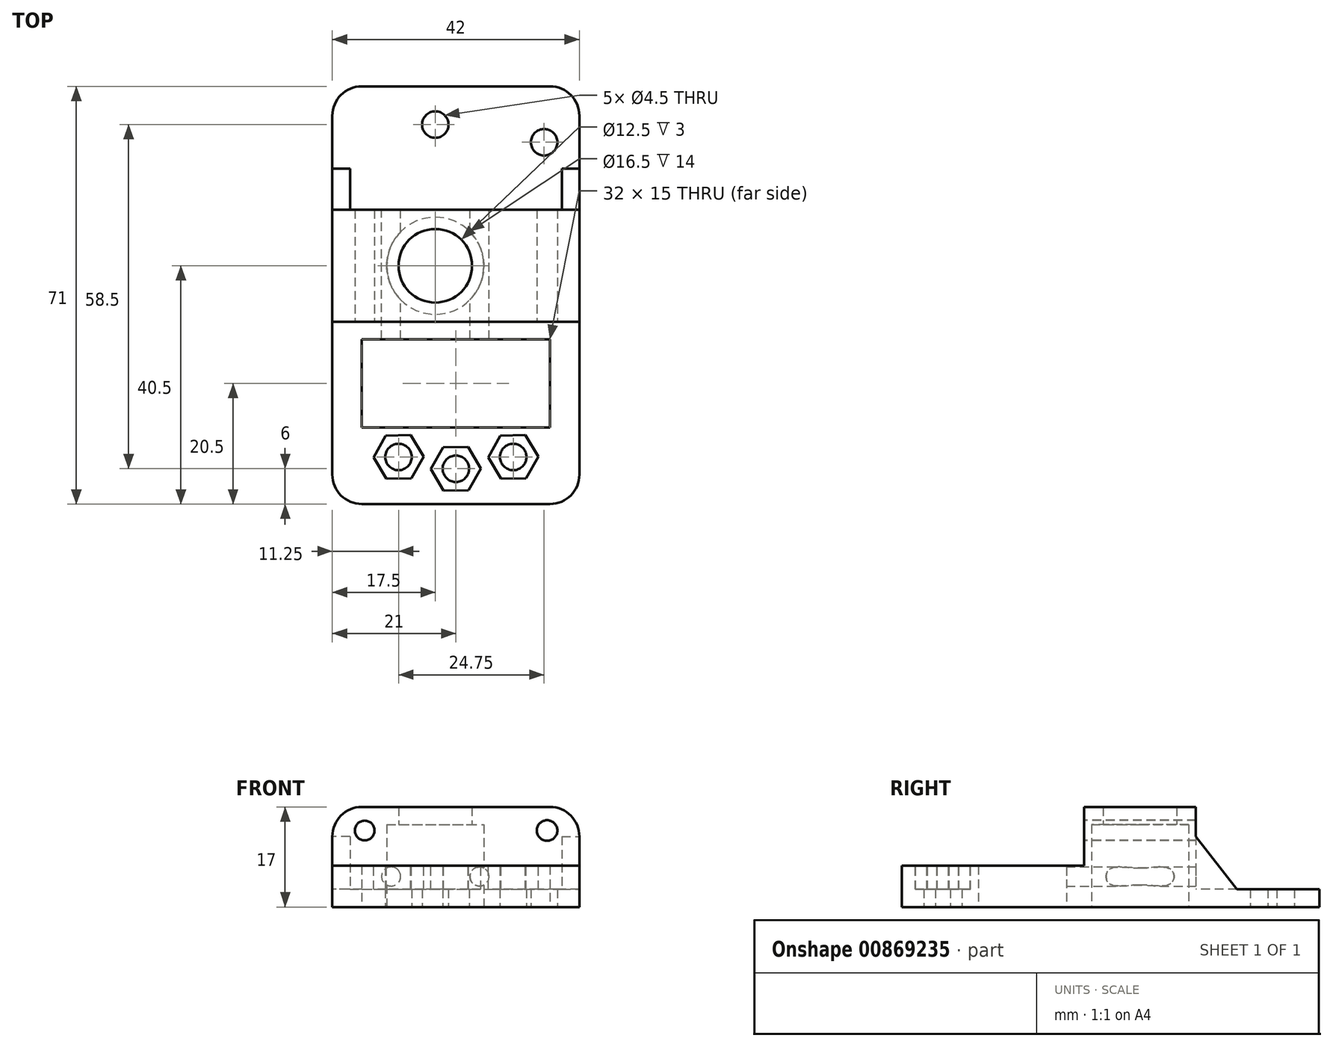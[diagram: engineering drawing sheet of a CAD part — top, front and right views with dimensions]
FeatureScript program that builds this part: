
annotation { "Feature Type Name" : "Feature", "Feature Type Description" : "" }
export const myFeature = defineFeature(function(context is Context, id is Id, definition is map)
    precondition{}
    {
        {
            var Q0;
            Q0=qCreatedBy(makeId("Top.planeOp"),FACE);
            var sketch = newSketch(context, id + "F0", { "sketchPlane" : qUnion([Q0])});
            skLineSegment(sketch, "E0.bottom", {"start": v(-21, 40) * mm, "end": v(21, 40) * mm});
            skLineSegment(sketch, "E0.top", {"start": v(-21, -31) * mm, "end": v(21, -31) * mm});
            skLineSegment(sketch, "E0.left", {"start": v(-21, 40) * mm, "end": v(-21, -31) * mm});
            skLineSegment(sketch, "E0.right", {"start": v(21, 40) * mm, "end": v(21, -31) * mm});
            skLineSegment(sketch, "E1", {"start": v(21, 0) * mm, "end": v(-21, 0) * mm});
            skLineSegment(sketch, "E2", {"start": v(-21, 19) * mm, "end": v(21, 19) * mm});
            skLineSegment(sketch, "E3.bottom", {"start": v(-16, -3) * mm, "end": v(16, -3) * mm});
            skLineSegment(sketch, "E3.top", {"start": v(-16, -18) * mm, "end": v(16, -18) * mm});
            skLineSegment(sketch, "E3.left", {"start": v(-16, -3) * mm, "end": v(-16, -18) * mm});
            skLineSegment(sketch, "E3.right", {"start": v(16, -3) * mm, "end": v(16, -18) * mm});
            skCircle(sketch, "E4", {"center": v(0, -25) * mm, "radius": 2.25 * mm});
            skCircle(sketch, "E5", {"center": v(-9.75, -23) * mm, "radius": 2.25 * mm});
            skCircle(sketch, "E6", {"center": v(9.75, -23) * mm, "radius": 2.25 * mm});
            skCircle(sketch, "E7", {"center": v(-3.5, 33.5) * mm, "radius": 2.25 * mm});
            skCircle(sketch, "E8", {"center": v(15, 30.5) * mm, "radius": 2.25 * mm});
            skLineSegment(sketch, "E9", {"start": v(-21, 9.5) * mm, "end": v(21, 9.5) * mm, "construction": true});
            skSolve(sketch);
        }
        {
            var Q0;
            {var subQ0=sQuery(id+"F0.wireOp",EDGE,"E0.top");Q0=makeQuery(id+"F0.imprint","IMPRINT",FACE,{"disambiguationData":[TD([[makeQuery(id+"F0.imprint","IMPRINT",EDGE,{"derivedFrom":subQ0}),1.0]])]});}
            extrude(context, id + "F1", {"entities" : qUnion([Q0]), "depth" : 7 * mm, "offsetDistance" : 25 * mm});
        }
        {
            var Q0;
            {var subQ0=sQuery(id+"F0.wireOp",EDGE,"E0.bottom");Q0=makeQuery(id+"F0.imprint","IMPRINT",FACE,{"disambiguationData":[TD([[makeQuery(id+"F0.imprint","IMPRINT",EDGE,{"derivedFrom":subQ0}),-1.0]])]});}
            extrude(context, id + "F2", {"entities" : qUnion([Q0]), "depth" : 3 * mm, "offsetDistance" : 25 * mm});
        }
        {
            var Q0;
            {var subQ0=sQuery(id+"F0.wireOp",EDGE,"E1");Q0=makeQuery(id+"F0.imprint","IMPRINT",FACE,{"disambiguationData":[TD([[makeQuery(id+"F0.imprint","IMPRINT",EDGE,{"derivedFrom":subQ0}),-1.0]])]});}
            extrude(context, id + "F3", {"entities" : qUnion([Q0]), "operationType" : NewBodyOperationType.ADD, "depth" : 17 * mm, "offsetDistance" : 25 * mm});
        }
        {
            var Q0;
            Q0=makeQuery(id+"F1.opExtrude","SWEPT_EDGE",EDGE,{"disambiguationData":[OSD([sQuery(id+"F0.wireOp",EDGE,"E0.top"),sQuery(id+"F0.wireOp",EDGE,"E0.left")])]});
            var Q1;
            Q1=makeQuery(id+"F1.opExtrude","SWEPT_EDGE",EDGE,{"disambiguationData":[OSD([sQuery(id+"F0.wireOp",EDGE,"E0.top"),sQuery(id+"F0.wireOp",EDGE,"E0.right")])]});
            fillet(context, id + "F4", {"entities" : qUnion([Q0, Q1]), "radius" : 5 * mm, "tangentPropagation" : true, "allowEdgeOverflow" : false});
        }
        {
            var Q0;
            Q0=makeQuery(id+"F2.opExtrude","SWEPT_EDGE",EDGE,{"disambiguationData":[OSD([sQuery(id+"F0.wireOp",EDGE,"E0.bottom"),sQuery(id+"F0.wireOp",EDGE,"E0.left")])]});
            var Q1;
            Q1=makeQuery(id+"F2.opExtrude","SWEPT_EDGE",EDGE,{"disambiguationData":[OSD([sQuery(id+"F0.wireOp",EDGE,"E0.bottom"),sQuery(id+"F0.wireOp",EDGE,"E0.right")])]});
            var Q2;
            Q2=makeQuery(id+"F3.opExtrude","CAP_EDGE",EDGE,{"disambiguationData":[OSD([sQuery(id+"F0.wireOp",EDGE,"E0.right")])],"isStart":false});
            var Q3;
            Q3=makeQuery(id+"F3.opExtrude","CAP_EDGE",EDGE,{"disambiguationData":[OSD([sQuery(id+"F0.wireOp",EDGE,"E0.left")])],"isStart":false});
            fillet(context, id + "F5", {"entities" : qUnion([Q0, Q1, Q2, Q3]), "radius" : 5 * mm, "tangentPropagation" : true, "allowEdgeOverflow" : false});
        }
        {
            var Q0;
            {var subQ0=sQuery(id+"F0.wireOp",EDGE,"E2");var subQ1=sQuery(id+"F0.wireOp",EDGE,"E1");var subQ2=sQuery(id+"F0.wireOp",EDGE,"E0.right");var subQ3=sQuery(id+"F0.wireOp",EDGE,"E0.left");Q0=makeQuery(id+"F3.boolean.opBoolean","MERGE",FACE,{"derivedFrom":[makeQuery(id+"F1.opExtrude","CAP_FACE",FACE,{"disambiguationData":[OSD([sQuery(id+"F0.wireOp",EDGE,"E0.top"),subQ3,subQ2,subQ1,sQuery(id+"F0.wireOp",EDGE,"E3.bottom"),sQuery(id+"F0.wireOp",EDGE,"E3.top"),sQuery(id+"F0.wireOp",EDGE,"E3.left"),sQuery(id+"F0.wireOp",EDGE,"E3.right")])],"isStart":true}),makeQuery(id+"F2.opExtrude","CAP_FACE",FACE,{"disambiguationData":[OSD([sQuery(id+"F0.wireOp",EDGE,"E0.bottom"),subQ3,subQ2,subQ0])],"isStart":true}),makeQuery(id+"F3.opExtrude","CAP_FACE",FACE,{"disambiguationData":[OSD([subQ3,subQ2,subQ1,subQ0])],"isStart":true})]});}
            var sketch = newSketch(context, id + "F6", { "sketchPlane" : qUnion([Q0])});
            skCircle(sketch, "E10", {"center": v(-3.5, -9.5) * mm, "radius": 6.25 * mm});
            skCircle(sketch, "E11", {"center": v(-3.5, -9.5) * mm, "radius": 8.25 * mm});
            skSolve(sketch);
        }
        {
            var Q0;
            Q0=makeQuery(id+"F6.imprint","IMPRINT",FACE,{"disambiguationData":[TD([[makeQuery(id+"F6.imprint","IMPRINT",EDGE,{"derivedFrom":sQuery(id+"F6.wireOp",EDGE,"E10")}),1.0]])]});
            extrude(context, id + "F7", {"entities" : qUnion([Q0]), "operationType" : NewBodyOperationType.REMOVE, "oppositeDirection" : true, "depth" : 25 * mm, "offsetDistance" : 25 * mm});
        }
        {
            var Q0;
            {var subQ0=sQuery(id+"F0.wireOp",EDGE,"E0.left");Q0=makeQuery(id+"F3.boolean.opBoolean","MERGE",FACE,{"derivedFrom":[makeQuery(id+"F1.opExtrude","SWEPT_FACE",FACE,{"disambiguationData":[OSD([subQ0])]}),makeQuery(id+"F2.opExtrude","SWEPT_FACE",FACE,{"disambiguationData":[OSD([subQ0])]}),makeQuery(id+"F3.opExtrude","SWEPT_FACE",FACE,{"disambiguationData":[OSD([subQ0])]})]});}
            var sketch = newSketch(context, id + "F8", { "sketchPlane" : qUnion([Q0])});
            skLineSegment(sketch, "E12", {"start": v(-19, 12) * mm, "end": v(-26, 3) * mm});
            skLineSegment(sketch, "E13", {"start": v(-26, 3) * mm, "end": v(-19, 3) * mm});
            skLineSegment(sketch, "E14", {"start": v(-19, 3) * mm, "end": v(-19, 12) * mm});
            skSolve(sketch);
        }
        {
            var Q0;
            Q0=makeQuery(id+"F8.imprint","IMPRINT",FACE,{"disambiguationData":[TD([[makeQuery(id+"F8.imprint","IMPRINT",EDGE,{"derivedFrom":sQuery(id+"F8.wireOp",EDGE,"E12")}),1.0]])]});
            extrude(context, id + "F9", {"entities" : qUnion([Q0]), "operationType" : NewBodyOperationType.ADD, "oppositeDirection" : true, "depth" : 3 * mm, "offsetDistance" : 25 * mm});
        }
        {
            var Q0;
            {var subQ0=sQuery(id+"F0.wireOp",EDGE,"E0.right");Q0=makeQuery(id+"F3.boolean.opBoolean","MERGE",FACE,{"derivedFrom":[makeQuery(id+"F1.opExtrude","SWEPT_FACE",FACE,{"disambiguationData":[OSD([subQ0])]}),makeQuery(id+"F2.opExtrude","SWEPT_FACE",FACE,{"disambiguationData":[OSD([subQ0])]}),makeQuery(id+"F3.opExtrude","SWEPT_FACE",FACE,{"disambiguationData":[OSD([subQ0])]})]});}
            var sketch = newSketch(context, id + "F10", { "sketchPlane" : qUnion([Q0])});
            skLineSegment(sketch, "E15", {"start": v(19, 12) * mm, "end": v(26, 3) * mm});
            skLineSegment(sketch, "E16", {"start": v(26, 3) * mm, "end": v(19, 3) * mm});
            skLineSegment(sketch, "E17", {"start": v(19, 3) * mm, "end": v(19, 12) * mm});
            skSolve(sketch);
        }
        {
            var Q0;
            Q0=makeQuery(id+"F10.imprint","IMPRINT",FACE,{"disambiguationData":[TD([[makeQuery(id+"F10.imprint","IMPRINT",EDGE,{"derivedFrom":sQuery(id+"F10.wireOp",EDGE,"E15")}),-1.0]])]});
            extrude(context, id + "F11", {"entities" : qUnion([Q0]), "operationType" : NewBodyOperationType.ADD, "oppositeDirection" : true, "depth" : 3 * mm, "offsetDistance" : 25 * mm});
        }
        {
            var Q0;
            Q0=makeQuery(id+"F3.opExtrude","SWEPT_FACE",FACE,{"disambiguationData":[OSD([sQuery(id+"F0.wireOp",EDGE,"E1")])]});
            var sketch = newSketch(context, id + "F12", { "sketchPlane" : qUnion([Q0])});
            skCircle(sketch, "E18", {"center": v(-15.5, 13) * mm, "radius": 1.68 * mm});
            skCircle(sketch, "E19", {"center": v(15.5, 13) * mm, "radius": 1.75 * mm});
            skSolve(sketch);
        }
        {
            var Q0;
            Q0 = qSketchRegion(id + "F12", true);
            extrude(context, id + "F13", {"entities" : qUnion([Q0]), "operationType" : NewBodyOperationType.REMOVE, "oppositeDirection" : true, "depth" : 25 * mm, "offsetDistance" : 25 * mm});
        }
        {
            var Q0;
            Q0 = qSketchRegion(id + "F6", true);
            var Q1;
            Q1=sQuery(id+"F6.wireOp",EDGE,"E11");
            extrude(context, id + "F14", {"entities" : qUnion([Q0]), "operationType" : NewBodyOperationType.REMOVE, "surfaceEntities" : qUnion([Q1]), "oppositeDirection" : true, "depth" : 14 * mm, "offsetDistance" : 25 * mm});
        }
        {
            var Q0;
            Q0=makeQuery(id+"F3.opExtrude","SWEPT_FACE",FACE,{"disambiguationData":[OSD([sQuery(id+"F0.wireOp",EDGE,"E2")])]});
            var sketch = newSketch(context, id + "F15", { "sketchPlane" : qUnion([Q0])});
            skCircle(sketch, "E20", {"center": v(-4, 5.19) * mm, "radius": 1.63 * mm});
            skCircle(sketch, "E21", {"center": v(11, 5.19) * mm, "radius": 1.63 * mm});
            skLineSegment(sketch, "E22", {"start": v(-4, 5.19) * mm, "end": v(11, 5.19) * mm, "construction": true});
            skPoint(sketch, "E23", {"position": v(3.5, 5.19) * mm});
            skSolve(sketch);
        }
        {
            var Q0;
            Q0=makeQuery(id+"F15.imprint","IMPRINT",FACE,{"disambiguationData":[TD([[makeQuery(id+"F15.imprint","IMPRINT",EDGE,{"derivedFrom":sQuery(id+"F15.wireOp",EDGE,"E20")}),1.0]])]});
            var Q1;
            Q1=makeQuery(id+"F15.imprint","IMPRINT",FACE,{"disambiguationData":[TD([[makeQuery(id+"F15.imprint","IMPRINT",EDGE,{"derivedFrom":sQuery(id+"F15.wireOp",EDGE,"E21")}),1.0]])]});
            extrude(context, id + "F16", {"entities" : qUnion([Q0, Q1]), "operationType" : NewBodyOperationType.REMOVE, "oppositeDirection" : true, "depth" : 30 * mm, "offsetDistance" : 25 * mm});
        }
        {
            var Q0;
            Q0=makeQuery(id+"F1.opExtrude","CAP_FACE",FACE,{"disambiguationData":[OSD([sQuery(id+"F0.wireOp",EDGE,"E0.top"),sQuery(id+"F0.wireOp",EDGE,"E0.left"),sQuery(id+"F0.wireOp",EDGE,"E0.right"),sQuery(id+"F0.wireOp",EDGE,"E1"),sQuery(id+"F0.wireOp",EDGE,"E3.bottom"),sQuery(id+"F0.wireOp",EDGE,"E3.top"),sQuery(id+"F0.wireOp",EDGE,"E3.left"),sQuery(id+"F0.wireOp",EDGE,"E3.right"),sQuery(id+"F0.wireOp",EDGE,"E4"),sQuery(id+"F0.wireOp",EDGE,"E5"),sQuery(id+"F0.wireOp",EDGE,"E6")])],"isStart":false});
            var sketch = newSketch(context, id + "F17", { "sketchPlane" : qUnion([Q0])});
            skCircle(sketch, "E24.cCircle", {"center": v(-9.75, -23) * mm, "radius": 4.25 * mm, "construction": true});
            skLineSegment(sketch, "E24.0", {"start": v(-7.69, -19.28) * mm, "end": v(-5.5, -22.93) * mm});
            skLineSegment(sketch, "E24.1", {"start": v(-5.5, -22.93) * mm, "end": v(-7.56, -26.64) * mm});
            skLineSegment(sketch, "E24.2", {"start": v(-7.56, -26.64) * mm, "end": v(-11.81, -26.72) * mm});
            skLineSegment(sketch, "E24.3", {"start": v(-11.81, -26.72) * mm, "end": v(-14, -23.07) * mm});
            skLineSegment(sketch, "E24.4", {"start": v(-14, -23.07) * mm, "end": v(-11.94, -19.36) * mm});
            skLineSegment(sketch, "E24.5", {"start": v(-11.94, -19.36) * mm, "end": v(-7.69, -19.28) * mm});
            skCircle(sketch, "E25.cCircle", {"center": v(0, -25) * mm, "radius": 4.25 * mm, "construction": true});
            skLineSegment(sketch, "E25.0", {"start": v(2.08, -21.3) * mm, "end": v(4.25, -24.95) * mm});
            skLineSegment(sketch, "E25.1", {"start": v(4.25, -24.95) * mm, "end": v(2.17, -28.65) * mm});
            skLineSegment(sketch, "E25.2", {"start": v(2.17, -28.65) * mm, "end": v(-2.08, -28.7) * mm});
            skLineSegment(sketch, "E25.3", {"start": v(-2.08, -28.7) * mm, "end": v(-4.25, -25.05) * mm});
            skLineSegment(sketch, "E25.4", {"start": v(-4.25, -25.05) * mm, "end": v(-2.17, -21.35) * mm});
            skLineSegment(sketch, "E25.5", {"start": v(-2.17, -21.35) * mm, "end": v(2.08, -21.3) * mm});
            skCircle(sketch, "E26.cCircle", {"center": v(9.75, -23) * mm, "radius": 4.25 * mm, "construction": true});
            skLineSegment(sketch, "E26.0", {"start": v(11.8, -19.28) * mm, "end": v(14, -22.92) * mm});
            skLineSegment(sketch, "E26.1", {"start": v(14, -22.92) * mm, "end": v(11.94, -26.64) * mm});
            skLineSegment(sketch, "E26.2", {"start": v(11.94, -26.64) * mm, "end": v(7.7, -26.72) * mm});
            skLineSegment(sketch, "E26.3", {"start": v(7.7, -26.72) * mm, "end": v(5.5, -23.08) * mm});
            skLineSegment(sketch, "E26.4", {"start": v(5.5, -23.08) * mm, "end": v(7.56, -19.36) * mm});
            skLineSegment(sketch, "E26.5", {"start": v(7.56, -19.36) * mm, "end": v(11.8, -19.28) * mm});
            skSolve(sketch);
        }
        {
            var Q0;
            Q0=makeQuery(id+"F17.imprint","IMPRINT",FACE,{"disambiguationData":[TD([[makeQuery(id+"F17.imprint","IMPRINT",EDGE,{"derivedFrom":sQuery(id+"F17.wireOp",EDGE,"E24.0")}),-1.0]])]});
            var Q1;
            Q1=makeQuery(id+"F17.imprint","IMPRINT",FACE,{"disambiguationData":[TD([[makeQuery(id+"F17.imprint","IMPRINT",EDGE,{"derivedFrom":sQuery(id+"F17.wireOp",EDGE,"E25.0")}),-1.0]])]});
            var Q2;
            Q2=makeQuery(id+"F17.imprint","IMPRINT",FACE,{"disambiguationData":[TD([[makeQuery(id+"F17.imprint","IMPRINT",EDGE,{"derivedFrom":sQuery(id+"F17.wireOp",EDGE,"E26.0")}),-1.0]])]});
            var Q3;
            Q3 = qConstructionFilter(qBodyType(qCreatedBy(id + "F17" ,EDGE), BodyType.WIRE), ConstructionObject.NO);
            extrude(context, id + "F18", {"entities" : qUnion([Q0, Q1, Q2]), "operationType" : NewBodyOperationType.REMOVE, "surfaceEntities" : qUnion([Q3]), "oppositeDirection" : true, "depth" : 4 * mm, "offsetDistance" : 25 * mm});
        }
    });
